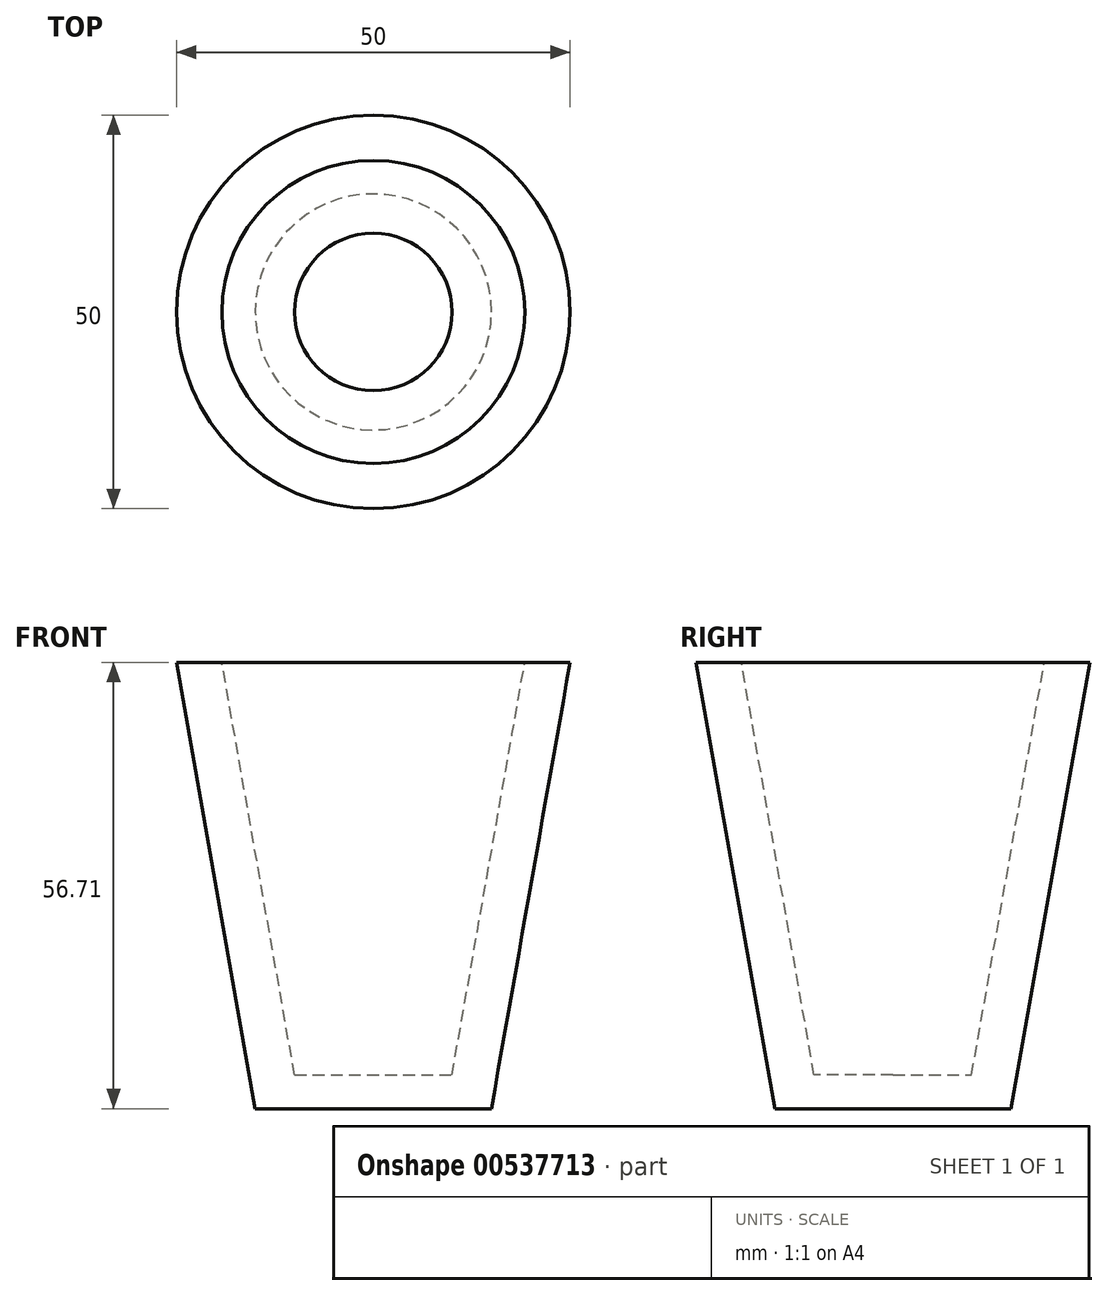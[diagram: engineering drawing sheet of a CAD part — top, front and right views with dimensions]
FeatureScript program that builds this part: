
annotation { "Feature Type Name" : "Feature", "Feature Type Description" : "" }
export const myFeature = defineFeature(function(context is Context, id is Id, definition is map)
    precondition{}
    {
        {
            var Q0;
            Q0=qCreatedBy(makeId("Front.planeOp"),FACE);
            var sketch = newSketch(context, id + "F0", { "sketchPlane" : qUnion([Q0])});
            skLineSegment(sketch, "E0", {"start": v(0, 46.62) * mm, "end": v(0, -41.08) * mm});
            skLineSegment(sketch, "E1", {"start": v(0, 35.99) * mm, "end": v(-25, 35.99) * mm});
            skLineSegment(sketch, "E2", {"start": v(-25, 35.99) * mm, "end": v(-15, -20.72) * mm});
            skLineSegment(sketch, "E3", {"start": v(-15, -20.72) * mm, "end": v(0, -20.72) * mm});
            skLineSegment(sketch, "E4", {"start": v(0, -20.72) * mm, "end": v(0, 35.99) * mm});
            skSolve(sketch);
        }
        {
            var Q0;
            Q0 = qSketchRegion(id + "F0", true);
            var Q1;
            Q1=sQuery(id+"F0.wireOp",EDGE,"E0");
            revolve(context, id + "F1", {"entities" : qUnion([Q0]), "axis" : qUnion([Q1]), "revolveType" : RevolveType.FULL});
        }
        {
            var Q0;
            Q0=qCreatedBy(makeId("Front.planeOp"),FACE);
            var sketch = newSketch(context, id + "F2", { "sketchPlane" : qUnion([Q0])});
            skLineSegment(sketch, "E5", {"start": v(0, 46.54) * mm, "end": v(0, -38.96) * mm});
            skLineSegment(sketch, "E6", {"start": v(0, 40.28) * mm, "end": v(-20, 40.28) * mm});
            skLineSegment(sketch, "E7", {"start": v(-20, 40.28) * mm, "end": v(-10, -16.43) * mm});
            skLineSegment(sketch, "E8", {"start": v(-10, -16.43) * mm, "end": v(0, -16.43) * mm});
            skLineSegment(sketch, "E9", {"start": v(0, -16.43) * mm, "end": v(0, 40.28) * mm});
            skSolve(sketch);
        }
        {
            var Q0;
            Q0 = qSketchRegion(id + "F2", true);
            var Q1;
            Q1=sQuery(id+"F2.wireOp",EDGE,"E5");
            revolve(context, id + "F3", {"operationType" : NewBodyOperationType.REMOVE, "entities" : qUnion([Q0]), "axis" : qUnion([Q1]), "revolveType" : RevolveType.FULL, "oppositeDirection" : true});
        }
    });
